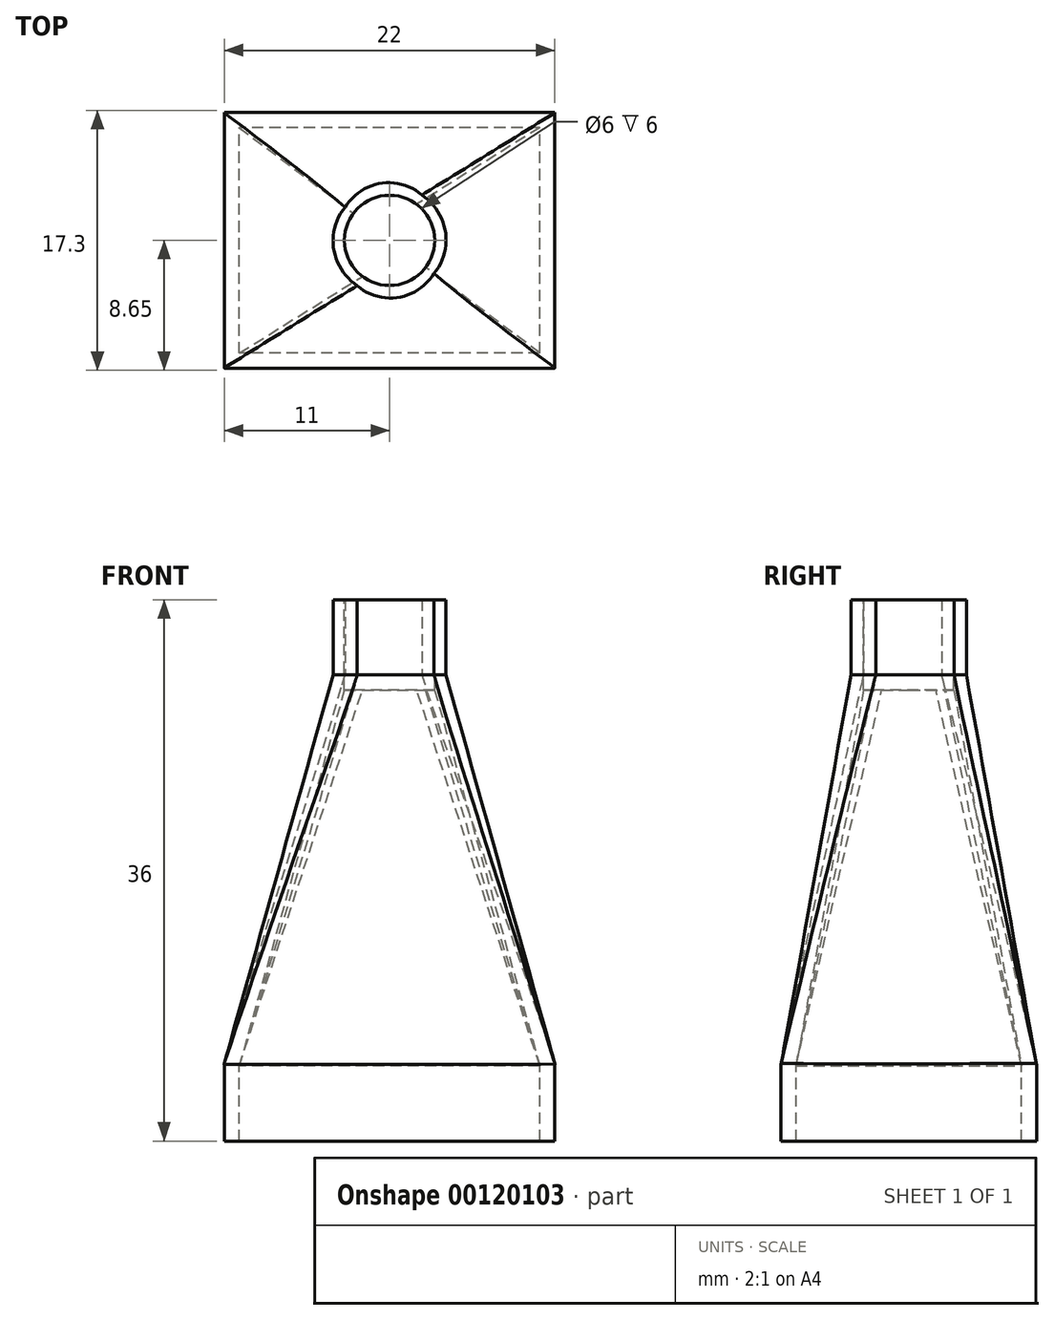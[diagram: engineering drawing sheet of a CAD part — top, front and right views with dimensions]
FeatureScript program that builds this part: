
annotation { "Feature Type Name" : "Feature", "Feature Type Description" : "" }
export const myFeature = defineFeature(function(context is Context, id is Id, definition is map)
    precondition{}
    {
        {
            var Q0;
            Q0=qCreatedBy(makeId("Top.planeOp"),FACE);
            var sketch = newSketch(context, id + "F0", { "sketchPlane" : qUnion([Q0])});
            skLineSegment(sketch, "E0.bottom", {"start": v(10, -7.5) * mm, "end": v(-10, -7.5) * mm});
            skLineSegment(sketch, "E0.top", {"start": v(10, 7.5) * mm, "end": v(-10, 7.5) * mm});
            skLineSegment(sketch, "E0.left", {"start": v(10, -7.5) * mm, "end": v(10, 7.5) * mm});
            skLineSegment(sketch, "E0.right", {"start": v(-10, -7.5) * mm, "end": v(-10, 7.5) * mm});
            skSolve(sketch);
        }
        {
            var Q0;
            Q0=makeQuery(id+"F0.imprint","IMPRINT",FACE,{"disambiguationData":[TD([[makeQuery(id+"F0.imprint","IMPRINT",EDGE,{"derivedFrom":sQuery(id+"F0.wireOp",EDGE,"E0.bottom")}),-1.0]])]});
            cPlane(context, id + "F1", {"entities" : qUnion([Q0]), "cplaneType" : CPlaneType.OFFSET, "offset" : 25 * mm, "width" : 150 * mm, "height" : 150 * mm});
        }
        {
            var Q0;
            Q0=qCreatedBy(id+"F1.planeOp",FACE);
            var sketch = newSketch(context, id + "F2", { "sketchPlane" : qUnion([Q0])});
            skCircle(sketch, "E1", {"center": v(0, 0) * mm, "radius": 3 * mm});
            skSolve(sketch);
        }
        {
            var Q0;
            Q0=makeQuery(id+"F0.imprint","IMPRINT",FACE,{"disambiguationData":[TD([[makeQuery(id+"F0.imprint","IMPRINT",EDGE,{"derivedFrom":sQuery(id+"F0.wireOp",EDGE,"E0.bottom")}),-1.0]])]});
            var Q1;
            Q1=makeQuery(id+"F2.imprint","IMPRINT",FACE,{"disambiguationData":[TD([[makeQuery(id+"F2.imprint","IMPRINT",EDGE,{"derivedFrom":sQuery(id+"F2.wireOp",EDGE,"E1")}),1.0]])]});
            var Q2;
            Q2=makeQuery(id+"F0.imprint","IMPRINT",FACE,{"disambiguationData":[TD([[makeQuery(id+"F0.imprint","IMPRINT",EDGE,{"derivedFrom":sQuery(id+"F0.wireOp",EDGE,"E0.bottom")}),-1.0]])]});
            var Q3;
            Q3=sQuery(id+"F2.wireOp",EDGE,"E1");
            loft(context, id + "F3", {"sheetProfilesArray" : [{ "sheetProfileEntities" : qUnion([Q0]) }, { "sheetProfileEntities" : qUnion([Q1]) }], "wireProfilesArray" : [{ "wireProfileEntities" : qUnion([Q2]) }, { "wireProfileEntities" : qUnion([Q3]) }]});
        }
        {
            var Q0;
            Q0=makeQuery(id+"F3.opLoft","CAP_FACE",FACE,{"disambiguationData":[OSD([makeQuery(id+"F0.imprint","IMPRINT",FACE,{"disambiguationData":[TD([[makeQuery(id+"F0.imprint","IMPRINT",EDGE,{"derivedFrom":sQuery(id+"F0.wireOp",EDGE,"E0.bottom")}),-1.0]])]})])],"isStart":true});
            extrude(context, id + "F4", {"entities" : qUnion([Q0]), "operationType" : NewBodyOperationType.ADD, "depth" : 5 * mm});
        }
        {
            var Q0;
            Q0=makeQuery(id+"F4.opExtrude","CAP_FACE",FACE,{"disambiguationData":[OSD([makeQuery(id+"F0.imprint","IMPRINT",FACE,{"disambiguationData":[TD([[makeQuery(id+"F0.imprint","IMPRINT",EDGE,{"derivedFrom":sQuery(id+"F0.wireOp",EDGE,"E0.bottom")}),-1.0]])]})])],"isStart":false});
            shell(context, id + "F5", {"entities" : qUnion([Q0]), "thickness" : 1 * mm, "oppositeDirection" : true});
        }
        {
            var Q0;
            Q0=makeQuery(id+"F3.opLoft","CAP_FACE",FACE,{"disambiguationData":[OSD([makeQuery(id+"F2.imprint","IMPRINT",FACE,{"disambiguationData":[TD([[makeQuery(id+"F2.imprint","IMPRINT",EDGE,{"derivedFrom":sQuery(id+"F2.wireOp",EDGE,"E1")}),1.0]])]})])],"isStart":true});
            var sketch = newSketch(context, id + "F6", { "sketchPlane" : qUnion([Q0])});
            skCircle(sketch, "E2", {"center": v(0, 0) * mm, "radius": 3 * mm});
            skSolve(sketch);
        }
        {
            var Q0;
            Q0 = qSketchRegion(id + "F6", true);
            extrude(context, id + "F7", {"entities" : qUnion([Q0]), "operationType" : NewBodyOperationType.REMOVE, "endBound" : BoundingType.THROUGH_ALL, "oppositeDirection" : true, "depth" : 25 * mm});
        }
        {
            var Q0;
            Q0=makeQuery(id+"F3.opLoft","CAP_FACE",FACE,{"disambiguationData":[OSD([makeQuery(id+"F2.imprint","IMPRINT",FACE,{"disambiguationData":[TD([[makeQuery(id+"F2.imprint","IMPRINT",EDGE,{"derivedFrom":sQuery(id+"F2.wireOp",EDGE,"E1")}),1.0]])]})])],"isStart":true});
            extrude(context, id + "F8", {"entities" : qUnion([Q0]), "operationType" : NewBodyOperationType.ADD, "depth" : 5 * mm});
        }
    });
